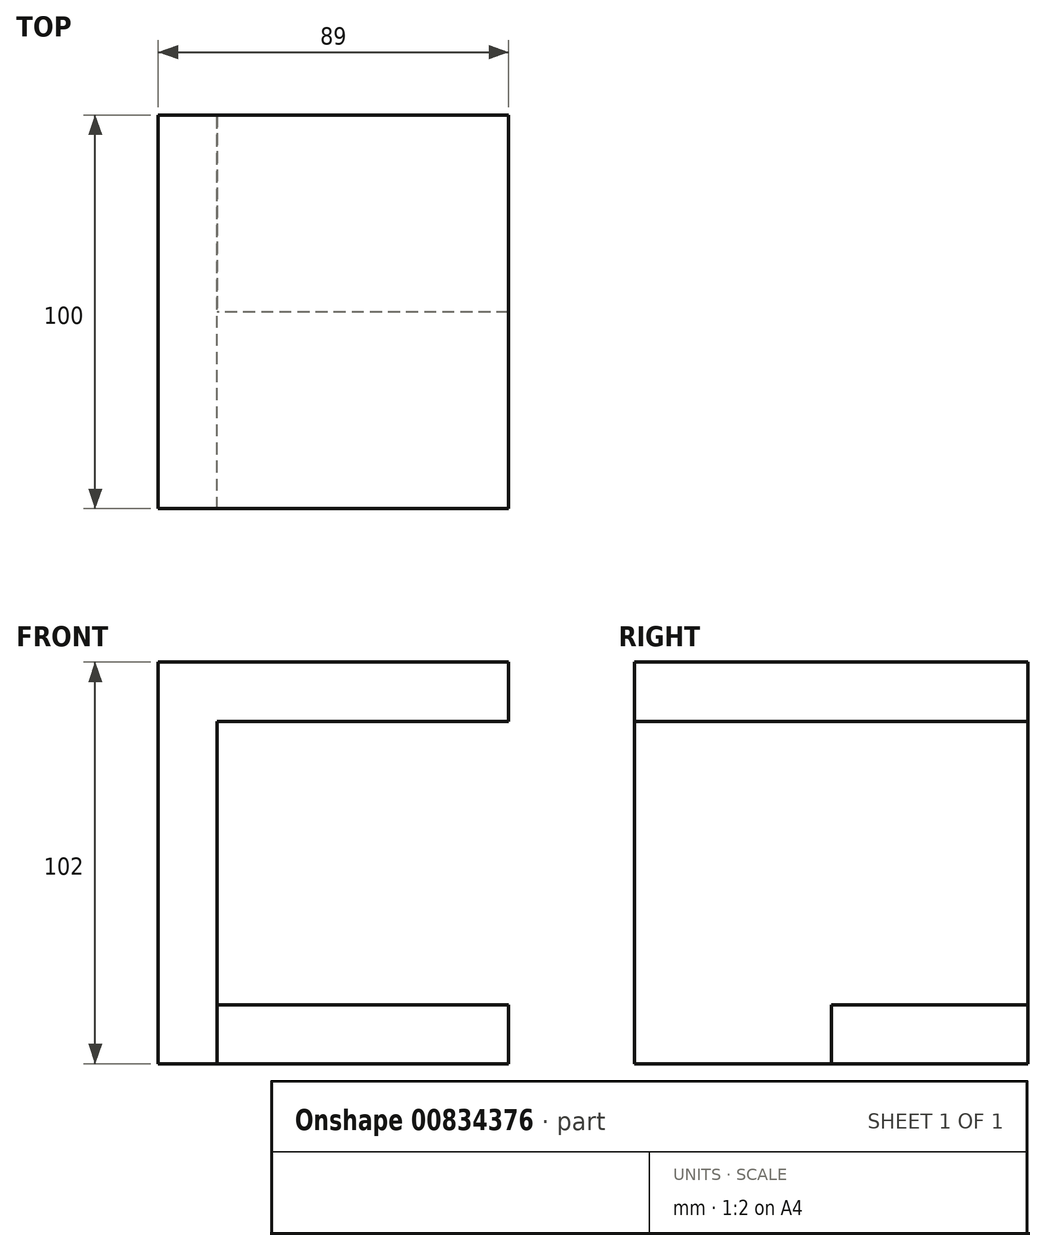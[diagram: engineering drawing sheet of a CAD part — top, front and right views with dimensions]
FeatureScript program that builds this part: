
annotation { "Feature Type Name" : "Feature", "Feature Type Description" : "" }
export const myFeature = defineFeature(function(context is Context, id is Id, definition is map)
    precondition{}
    {
        {
            var Q0;
            Q0=qCreatedBy(makeId("Front.planeOp"),FACE);
            var sketch = newSketch(context, id + "F0", { "sketchPlane" : qUnion([Q0])});
            skLineSegment(sketch, "E0", {"start": v(0, 0) * mm, "end": v(0, 87) * mm});
            skLineSegment(sketch, "E1", {"start": v(0, 87) * mm, "end": v(74, 87) * mm});
            skLineSegment(sketch, "E2", {"start": v(74, 87) * mm, "end": v(74, 102) * mm});
            skLineSegment(sketch, "E3", {"start": v(74, 102) * mm, "end": v(-15, 102) * mm});
            skLineSegment(sketch, "E4", {"start": v(-15, 102) * mm, "end": v(-15, 0) * mm});
            skLineSegment(sketch, "E5", {"start": v(-15, 0) * mm, "end": v(0, 0) * mm});
            skSolve(sketch);
        }
        {
            var Q0;
            Q0=makeQuery(id+"F0.imprint","IMPRINT",FACE,{"disambiguationData":[TD([[makeQuery(id+"F0.imprint","IMPRINT",EDGE,{"derivedFrom":sQuery(id+"F0.wireOp",EDGE,"E0")}),1.0]])]});
            extrude(context, id + "F1", {"entities" : qUnion([Q0]), "depth" : 100 * mm, "offsetDistance" : 25 * mm});
        }
        {
            var Q0;
            Q0=makeQuery(id+"F1.opExtrude","SWEPT_FACE",FACE,{"disambiguationData":[OSD([sQuery(id+"F0.wireOp",EDGE,"E0")])]});
            var sketch = newSketch(context, id + "F2", { "sketchPlane" : qUnion([Q0])});
            skLineSegment(sketch, "E6.bottom", {"start": v(0, 0) * mm, "end": v(-50, 0) * mm});
            skLineSegment(sketch, "E6.top", {"start": v(0, 15) * mm, "end": v(-50, 15) * mm});
            skLineSegment(sketch, "E6.left", {"start": v(0, 0) * mm, "end": v(0, 15) * mm});
            skLineSegment(sketch, "E6.right", {"start": v(-50, 0) * mm, "end": v(-50, 15) * mm});
            skSolve(sketch);
        }
        {
            var Q0;
            Q0=makeQuery(id+"F2.imprint","IMPRINT",FACE,{"disambiguationData":[TD([[makeQuery(id+"F2.imprint","IMPRINT",EDGE,{"derivedFrom":sQuery(id+"F2.wireOp",EDGE,"E6.bottom")}),1.0]])]});
            extrude(context, id + "F3", {"entities" : qUnion([Q0]), "operationType" : NewBodyOperationType.ADD, "depth" : 74 * mm, "offsetDistance" : 25 * mm});
        }
    });
